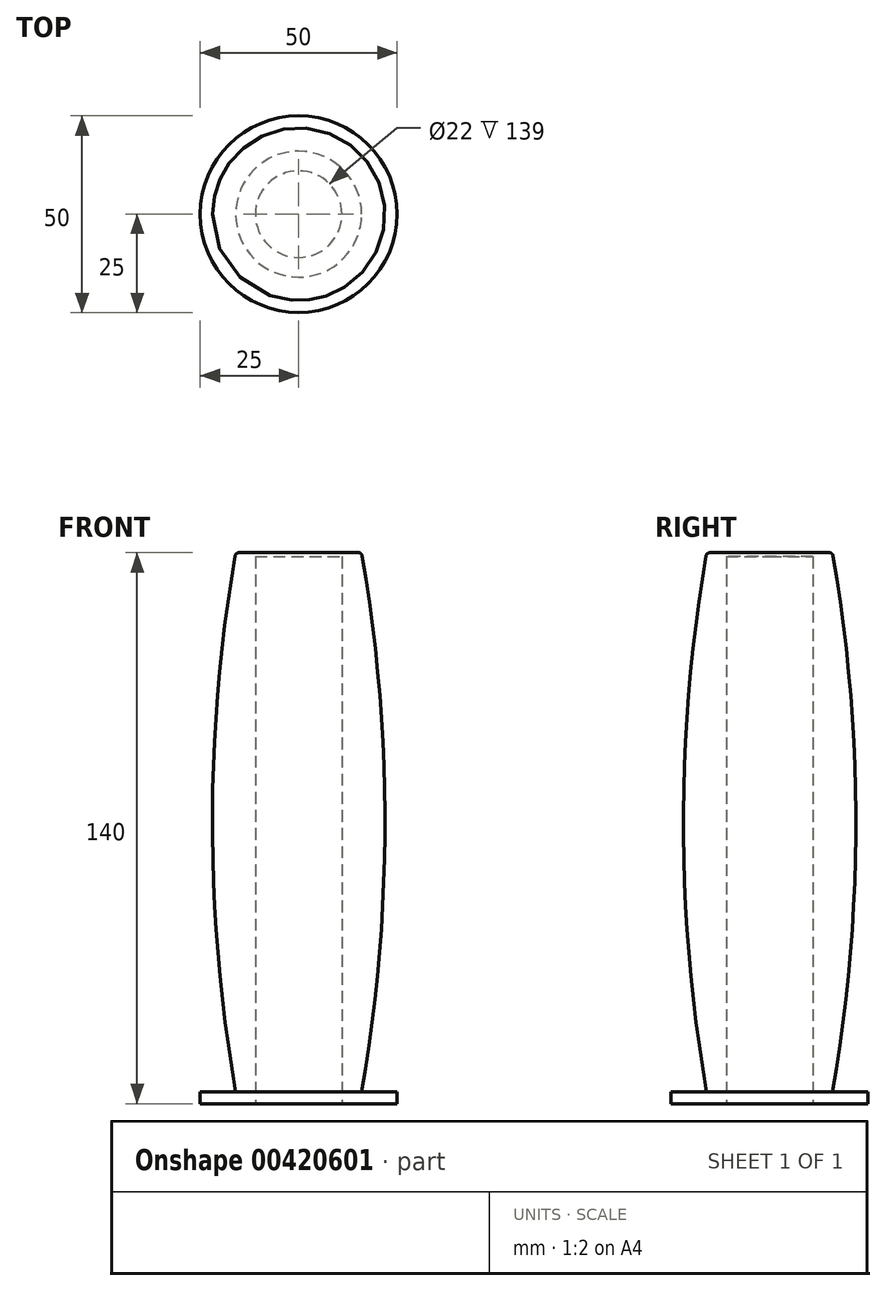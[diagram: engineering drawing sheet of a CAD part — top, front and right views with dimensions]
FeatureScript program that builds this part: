
annotation { "Feature Type Name" : "Feature", "Feature Type Description" : "" }
export const myFeature = defineFeature(function(context is Context, id is Id, definition is map)
    precondition{}
    {
        {
            var Q0;
            Q0=qCreatedBy(makeId("Front.planeOp"),FACE);
            var sketch = newSketch(context, id + "F0", { "sketchPlane" : qUnion([Q0])});
            skLineSegment(sketch, "E0", {"start": v(0, 0) * mm, "end": v(0, 69.73) * mm, "construction": true});
            skLineSegment(sketch, "E1", {"start": v(-25, 0) * mm, "end": v(-25, 3) * mm});
            skLineSegment(sketch, "E2", {"start": v(-25, 3) * mm, "end": v(-16, 3) * mm});
            skLineSegment(sketch, "E3", {"start": v(-11, 140) * mm, "end": v(-11, 0) * mm, "construction": true});
            skLineSegment(sketch, "E4", {"start": v(-11, 0) * mm, "end": v(-25, 0) * mm});
            skLineSegment(sketch, "E5", {"start": v(-16, 3) * mm, "end": v(-16, 140) * mm, "construction": true});
            skLineSegment(sketch, "E6", {"start": v(-11, 140) * mm, "end": v(-16, 140) * mm});
            skArc(sketch, "E7", {"start": v(-16, 140) * mm, "mid": v(-21.9, 71.5) * mm, "end": v(-16, 3) * mm});
            skLineSegment(sketch, "E8", {"start": v(-11, 140) * mm, "end": v(0, 140) * mm});
            skLineSegment(sketch, "E9", {"start": v(0, 140) * mm, "end": v(0, 139) * mm});
            skLineSegment(sketch, "E10", {"start": v(0, 139) * mm, "end": v(-11, 139) * mm});
            skLineSegment(sketch, "E11", {"start": v(-11, 139) * mm, "end": v(-11, 0) * mm});
            skSolve(sketch);
        }
        {
            var Q0;
            Q0 = qSketchRegion(id + "F0", true);
            var Q1;
            Q1=sQuery(id+"F0.wireOp",EDGE,"E0");
            revolve(context, id + "F1", {"entities" : qUnion([Q0]), "axis" : qUnion([Q1]), "revolveType" : RevolveType.FULL});
        }
        {
            var Q0;
            Q0=makeQuery(id+"F1.opRevolve","SWEPT_EDGE",EDGE,{"disambiguationData":[OSD([sQuery(id+"F0.wireOp",EDGE,"E5"),sQuery(id+"F0.wireOp",EDGE,"E6")])]});
            var Q1;
            Q1=makeQuery(id+"F1.opRevolve","SWEPT_EDGE",EDGE,{"disambiguationData":[OSD([sQuery(id+"F0.wireOp",EDGE,"E3"),sQuery(id+"F0.wireOp",EDGE,"E6")])]});
            fillet(context, id + "F2", {"entities" : qUnion([Q0, Q1]), "radius" : 1 * mm, "tangentPropagation" : true, "allowEdgeOverflow" : false});
        }
    });
